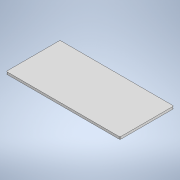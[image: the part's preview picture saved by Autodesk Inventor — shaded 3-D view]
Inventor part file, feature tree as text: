
AUTODESK INVENTOR PART (.ipt)
format: ipt  version: 2021 (Build 250183000, 183)  size: 101,888 bytes
history: native  units: mm
features: extrude x1, sketch x1
ambient origin geometry x8: Origin, YZ Plane, XZ Plane, XY Plane, X Axis, Y Axis, Z Axis, Center Point
bodies: Solid1 (feature_tree)
feature tree (2):
  extrude  "Extrusion1"  Depth=116.2mm
  sketch  "Sketch1"  dims[d0=246.0mm d1=116.2mm d2=5.0mm d3=0.0mm d4=2.0mm]
